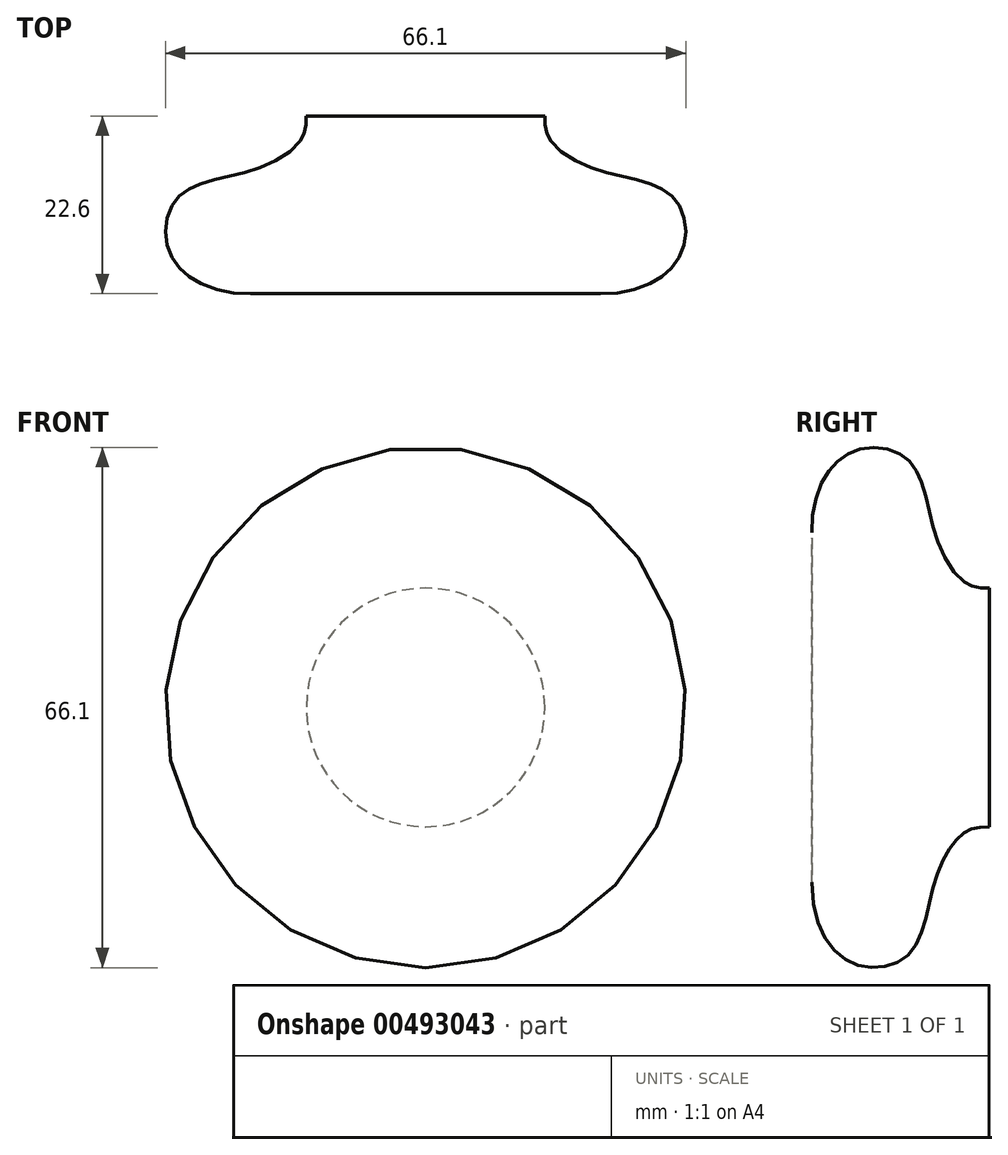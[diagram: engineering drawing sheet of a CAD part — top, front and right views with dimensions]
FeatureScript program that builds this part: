
annotation { "Feature Type Name" : "Feature", "Feature Type Description" : "" }
export const myFeature = defineFeature(function(context is Context, id is Id, definition is map)
    precondition{}
    {
        {
            var Q0;
            Q0=qCreatedBy(makeId("Top.planeOp"),FACE);
            var sketch = newSketch(context, id + "F0", { "sketchPlane" : qUnion([Q0])});
            skLineSegment(sketch, "E0", {"start": v(0, 0) * mm, "end": v(0, -22.6) * mm, "construction": true});
            skLineSegment(sketch, "E1", {"start": v(0, -22.6) * mm, "end": v(22.23, -22.6) * mm});
            skFitSpline(sketch, "E2", {"points": [v(22.23, -22.6) * mm, v(32.59, -17.19) * mm, v(31.22, -10.14) * mm, v(22.23, -6.98) * mm, v(16.07, -3.42) * mm, v(15.15, 0) * mm], "startDerivative": vector(66.8, 0) * mm, "endDerivative": vector(0, 31.22) * mm});
            skLineSegment(sketch, "E3", {"start": v(15.15, 0) * mm, "end": v(0, 0) * mm});
            skLineSegment(sketch, "E4", {"start": v(0, -22.6) * mm, "end": v(0, 0) * mm});
            skSolve(sketch);
        }
        {
            var Q0;
            Q0=qSketchRegion(id+"F0",true);
            var Q1;
            Q1=sQuery(id+"F0.wireOp",EDGE,"E4");
            revolve(context, id + "F1", {"entities" : qUnion([Q0]), "axis" : qUnion([Q1]), "revolveType" : RevolveType.FULL});
        }
    });
